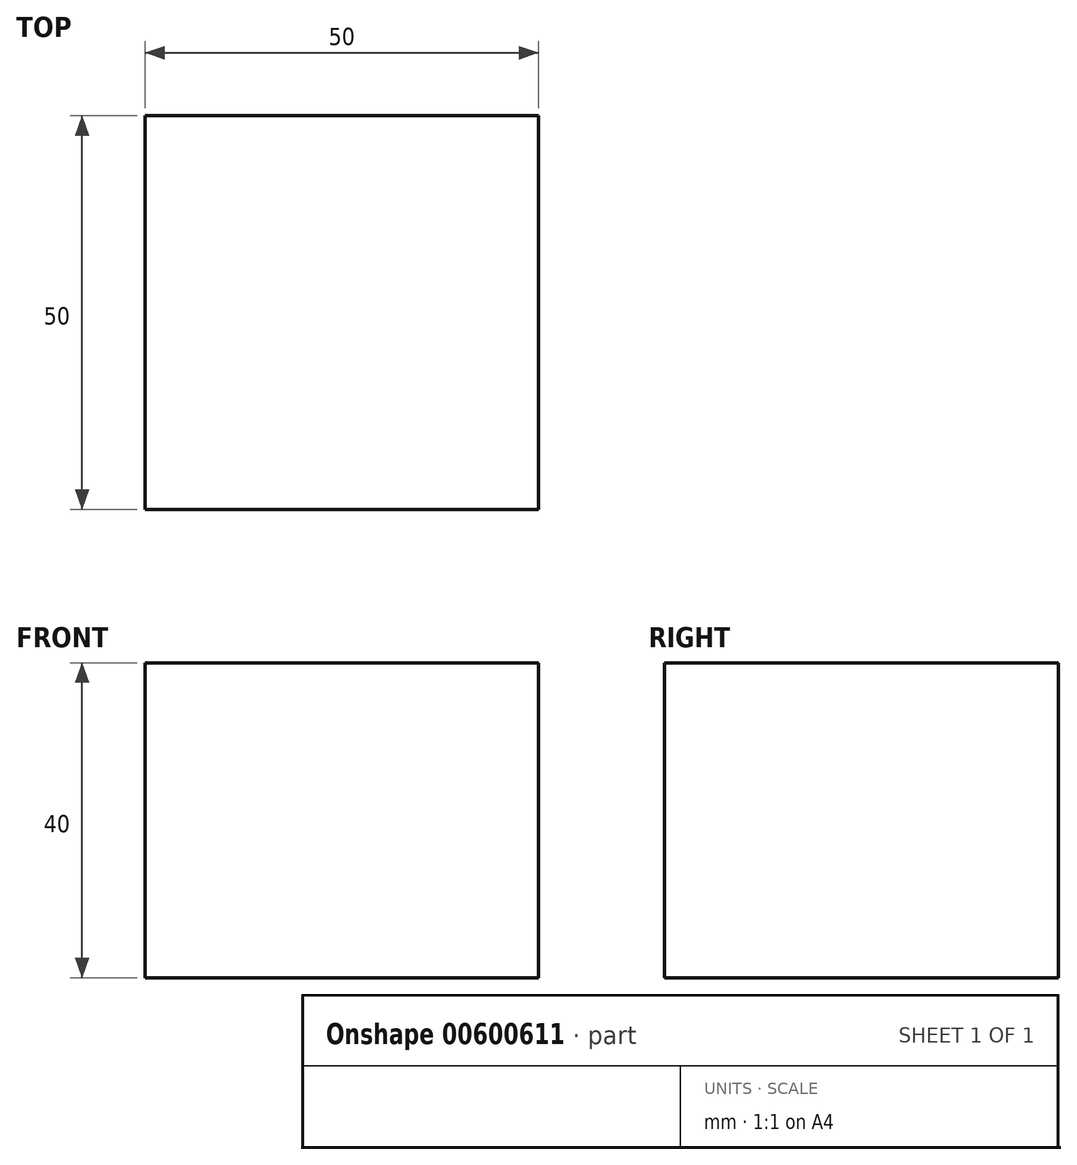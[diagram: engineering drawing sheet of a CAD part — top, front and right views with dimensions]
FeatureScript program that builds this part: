
annotation { "Feature Type Name" : "Feature", "Feature Type Description" : "" }
export const myFeature = defineFeature(function(context is Context, id is Id, definition is map)
    precondition{}
    {
        {
            var Q0;
            Q0=qCreatedBy(makeId("Top.planeOp"),FACE);
            var sketch = newSketch(context, id + "F0", { "sketchPlane" : qUnion([Q0])});
            skLineSegment(sketch, "E0.bottom", {"start": v(-18.37, 14.46) * mm, "end": v(31.63, 14.46) * mm});
            skLineSegment(sketch, "E0.top", {"start": v(-18.37, -35.54) * mm, "end": v(31.63, -35.54) * mm});
            skLineSegment(sketch, "E0.left", {"start": v(-18.37, 14.46) * mm, "end": v(-18.37, -35.54) * mm});
            skLineSegment(sketch, "E0.right", {"start": v(31.63, 14.46) * mm, "end": v(31.63, -35.54) * mm});
            skSolve(sketch);
        }
        {
            var Q0;
            Q0=makeQuery(id+"F0.imprint","IMPRINT",FACE,{"disambiguationData":[TD([[makeQuery(id+"F0.imprint","IMPRINT",EDGE,{"derivedFrom":sQuery(id+"F0.wireOp",EDGE,"E0.bottom")}),-1.0]])]});
            extrude(context, id + "F1", {"entities" : qUnion([Q0]), "depth" : 40 * mm, "offsetDistance" : 25 * mm});
        }
    });
